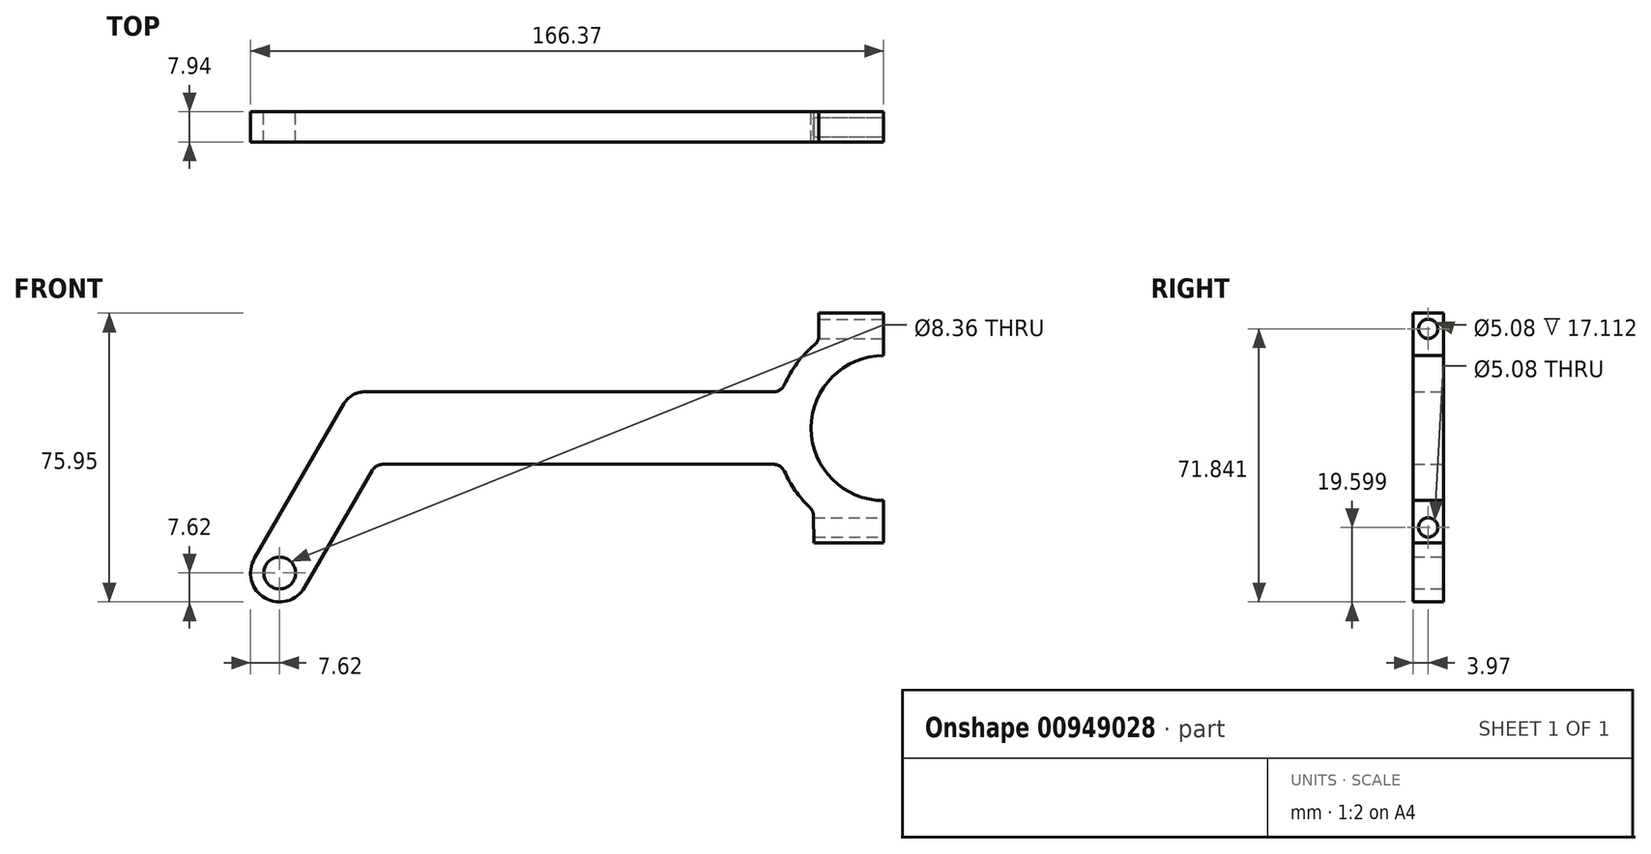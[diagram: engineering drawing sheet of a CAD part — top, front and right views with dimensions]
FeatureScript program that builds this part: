
annotation { "Feature Type Name" : "Feature", "Feature Type Description" : "" }
export const myFeature = defineFeature(function(context is Context, id is Id, definition is map)
    precondition{}
    {
        {
            var Q0;
            Q0=qCreatedBy(makeId("Front.planeOp"),FACE);
            var sketch = newSketch(context, id + "F0", { "sketchPlane" : qUnion([Q0])});
            skArc(sketch, "E0", {"start": v(0, 19.05) * mm, "mid": v(-19.05, 0) * mm, "end": v(0, -19.05) * mm});
            skCircle(sketch, "E1", {"center": v(-158.75, -38.1) * mm, "radius": 4.18 * mm});
            skArc(sketch, "E2", {"start": v(-18.17, 21.89) * mm, "mid": v(-22.72, 17.12) * mm, "end": v(-26.05, 11.42) * mm});
            skLineSegment(sketch, "E3", {"start": v(0, 30.23) * mm, "end": v(-17.02, 30.23) * mm});
            skLineSegment(sketch, "E4", {"start": v(-17.02, 30.23) * mm, "end": v(-17.02, 24.33) * mm});
            skLineSegment(sketch, "E5", {"start": v(0, -30.23) * mm, "end": v(-18.27, -30.23) * mm});
            skLineSegment(sketch, "E6", {"start": v(0, 30.23) * mm, "end": v(0, 19.05) * mm});
            skLineSegment(sketch, "E7", {"start": v(0, -19.05) * mm, "end": v(0, -30.23) * mm});
            skLineSegment(sketch, "E8", {"start": v(-28.96, 9.53) * mm, "end": v(-136.39, 9.52) * mm});
            skPoint(sketch, "E9.newPointA", {"position": v(-14.16, 24.68) * mm});
            skArc(sketch, "E10", {"start": v(-26.05, -11.42) * mm, "mid": v(-23.23, -16.42) * mm, "end": v(-19.46, -20.75) * mm});
            skLineSegment(sketch, "E11", {"start": v(-18.27, -30.23) * mm, "end": v(-18.45, -22.99) * mm});
            skPoint(sketch, "E12.newPointA", {"position": v(-17.02, 21.98) * mm});
            skPoint(sketch, "E12.newPointB", {"position": v(-18.06, 21.98) * mm});
            skArc(sketch, "E12.filletArc", {"start": v(-18.17, 21.89) * mm, "mid": v(-17.32, 22.98) * mm, "end": v(-17.02, 24.33) * mm});
            skPoint(sketch, "E13.visualSharp", {"position": v(-26.8, 9.53) * mm});
            skArc(sketch, "E13.filletArc", {"start": v(-28.96, 9.53) * mm, "mid": v(-27.22, 10.04) * mm, "end": v(-26.05, 11.42) * mm});
            skLineSegment(sketch, "E14", {"start": v(-28.96, -9.52) * mm, "end": v(-131.63, -9.53) * mm});
            skArc(sketch, "E15", {"start": v(-165.35, -34.3) * mm, "mid": v(-162.56, -44.7) * mm, "end": v(-152.15, -41.91) * mm});
            skLineSegment(sketch, "E16", {"start": v(-165.35, -34.3) * mm, "end": v(-141.89, 6.35) * mm});
            skLineSegment(sketch, "E17", {"start": v(-152.15, -41.91) * mm, "end": v(-134.38, -11.11) * mm});
            skArc(sketch, "E18.filletArc", {"start": v(-136.39, 9.52) * mm, "mid": v(-139.56, 8.67) * mm, "end": v(-141.89, 6.35) * mm});
            skPoint(sketch, "E19.visualSharp", {"position": v(-133.46, -9.53) * mm});
            skArc(sketch, "E19.filletArc", {"start": v(-131.63, -9.53) * mm, "mid": v(-133.22, -9.95) * mm, "end": v(-134.38, -11.11) * mm});
            skPoint(sketch, "E20.visualSharp", {"position": v(-26.8, -9.52) * mm});
            skArc(sketch, "E20.filletArc", {"start": v(-26.05, -11.42) * mm, "mid": v(-27.22, -10.04) * mm, "end": v(-28.96, -9.52) * mm});
            skPoint(sketch, "E21.newPointA", {"position": v(-18.6, -21.53) * mm});
            skPoint(sketch, "E21.newPointB", {"position": v(-18.5, -21.53) * mm});
            skArc(sketch, "E21.filletArc", {"start": v(-18.45, -22.99) * mm, "mid": v(-18.73, -21.77) * mm, "end": v(-19.46, -20.75) * mm});
            skSolve(sketch);
        }
        {
            var Q0;
            Q0=makeQuery(id+"F0.imprint","IMPRINT",FACE,{"disambiguationData":[TD([[makeQuery(id+"F0.imprint","IMPRINT",EDGE,{"derivedFrom":sQuery(id+"F0.wireOp",EDGE,"E0")}),-1.0]])]});
            extrude(context, id + "F1", {"entities" : qUnion([Q0]), "endBound" : BoundingType.SYMMETRIC, "depth" : 7.94 * mm, "offsetDistance" : 25.4 * mm});
        }
        {
            var Q0;
            Q0=qCreatedBy(makeId("Right.planeOp"),FACE);
            var sketch = newSketch(context, id + "F2", { "sketchPlane" : qUnion([Q0])});
            skPoint(sketch, "E22", {"position": v(0, 26.12) * mm});
            skPoint(sketch, "E23", {"position": v(0, -26.12) * mm});
            skSolve(sketch);
        }
        {
            var Q0;
            Q0=sQuery(id+"F2.wireOp",VERTEX,"E22");
            var Q1;
            Q1=sQuery(id+"F2.wireOp",VERTEX,"E23");
            var Q2;
            Q2=makeQuery(id+"F1.opExtrude","SWEPT_BODY",BODY,{"disambiguationData":[OSD([sQuery(id+"F0.wireOp",EDGE,"E0"),sQuery(id+"F0.wireOp",EDGE,"E1"),sQuery(id+"F0.wireOp",EDGE,"E2"),sQuery(id+"F0.wireOp",EDGE,"E3"),sQuery(id+"F0.wireOp",EDGE,"E4"),sQuery(id+"F0.wireOp",EDGE,"E5"),sQuery(id+"F0.wireOp",EDGE,"E6"),sQuery(id+"F0.wireOp",EDGE,"E7"),sQuery(id+"F0.wireOp",EDGE,"E8"),sQuery(id+"F0.wireOp",EDGE,"E10"),sQuery(id+"F0.wireOp",EDGE,"E11"),sQuery(id+"F0.wireOp",EDGE,"E12.filletArc"),sQuery(id+"F0.wireOp",EDGE,"E13.filletArc"),sQuery(id+"F0.wireOp",EDGE,"E14"),sQuery(id+"F0.wireOp",EDGE,"E15"),sQuery(id+"F0.wireOp",EDGE,"E16"),sQuery(id+"F0.wireOp",EDGE,"E17"),sQuery(id+"F0.wireOp",EDGE,"E18.filletArc"),sQuery(id+"F0.wireOp",EDGE,"E19.filletArc"),sQuery(id+"F0.wireOp",EDGE,"E20.filletArc"),sQuery(id+"F0.wireOp",EDGE,"E21.filletArc")])]});
            hole(context, id + "F3", {"style" : HoleStyle.SIMPLE, "endStyle" : HoleEndStyle.BLIND, "holeDiameter" : 5.08 * mm, "majorDiameter" : 6.35 * mm, "holeDepth" : 25.4 * mm, "isTappedThrough" : true, "tappedDepth" : 12.7 * mm, "tapClearance" : 3, "locations" : qUnion([Q0, Q1]), "scope" : qUnion([Q2])});
        }
    });
